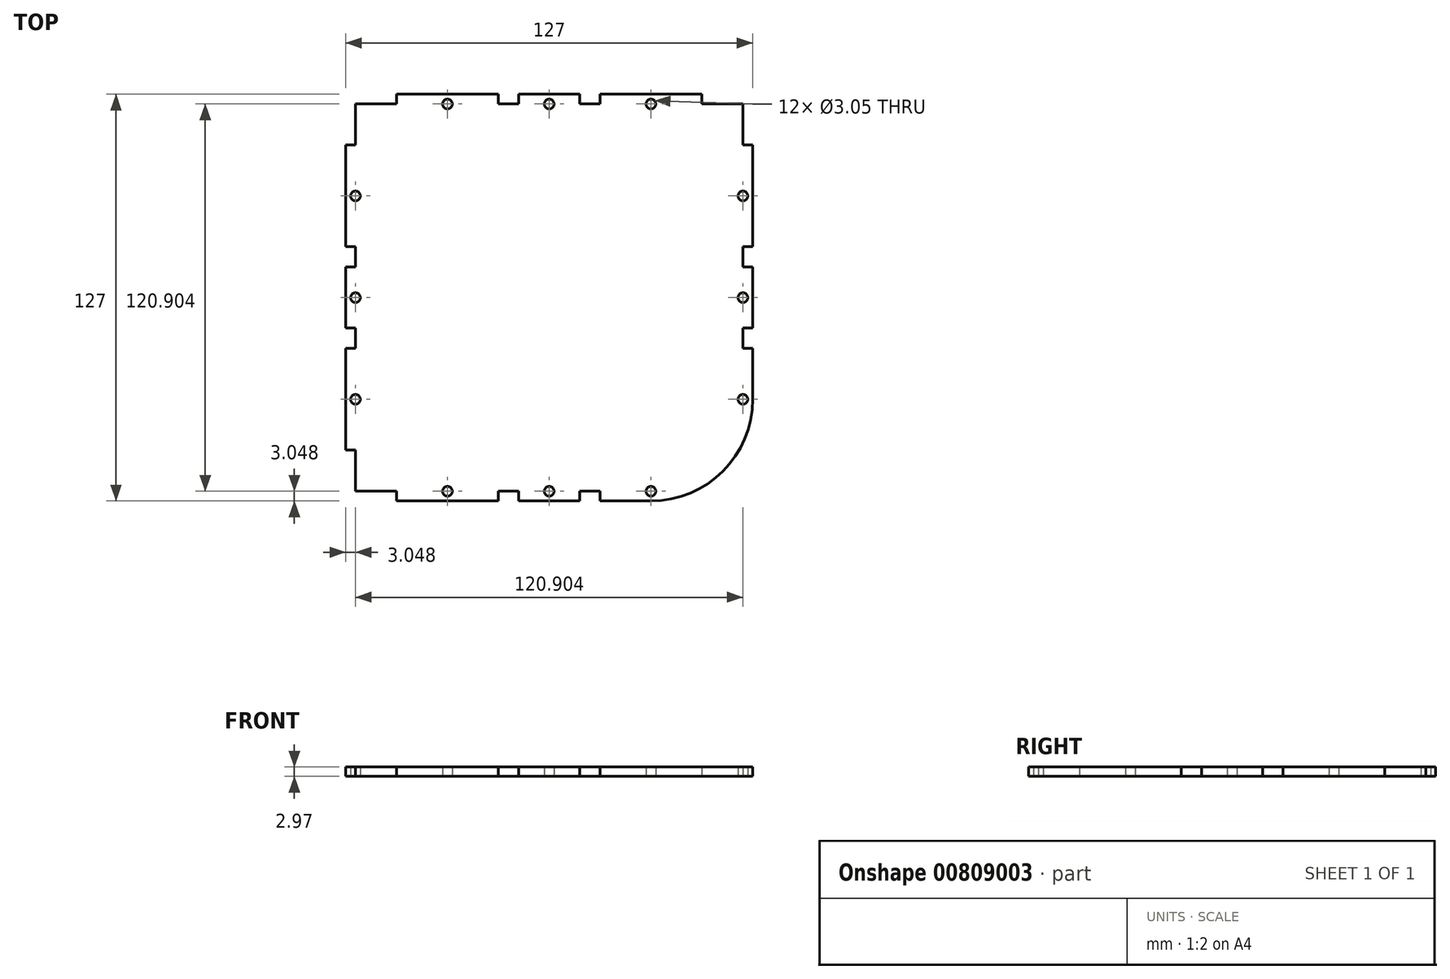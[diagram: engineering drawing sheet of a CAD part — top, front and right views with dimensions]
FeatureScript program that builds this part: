
annotation { "Feature Type Name" : "Feature", "Feature Type Description" : "" }
export const myFeature = defineFeature(function(context is Context, id is Id, definition is map)
    precondition{}
    {
        {
            var Q0;
            Q0=qCreatedBy(makeId("Top.planeOp"),FACE);
            var sketch = newSketch(context, id + "F0", { "sketchPlane" : qUnion([Q0])});
            skLineSegment(sketch, "E0", {"start": v(0, 76.16) * mm, "end": v(0, -68.5) * mm, "construction": true});
            skLineSegment(sketch, "E1", {"start": v(-81.79, 0) * mm, "end": v(75, 0) * mm, "construction": true});
            skLineSegment(sketch, "E2.right", {"start": v(63.5, 47.62) * mm, "end": v(63.5, 15.88) * mm});
            skLineSegment(sketch, "E3", {"start": v(-60.45, 78.6) * mm, "end": v(-60.45, -79.5) * mm, "construction": true});
            skLineSegment(sketch, "E4", {"start": v(-79.62, 60.45) * mm, "end": v(85.22, 60.45) * mm, "construction": true});
            skLineSegment(sketch, "E5", {"start": v(60.45, 79.72) * mm, "end": v(60.45, -47.62) * mm, "construction": true});
            skLineSegment(sketch, "E6", {"start": v(-81.64, -60.45) * mm, "end": v(47.63, -60.45) * mm, "construction": true});
            skCircle(sketch, "E7", {"center": v(0, 60.45) * mm, "radius": 1.52 * mm});
            skCircle(sketch, "E8", {"center": v(-60.45, 0) * mm, "radius": 1.52 * mm});
            skCircle(sketch, "E9", {"center": v(60.45, 0) * mm, "radius": 1.52 * mm});
            skCircle(sketch, "E10", {"center": v(0, -60.45) * mm, "radius": 1.52 * mm});
            skCircle(sketch, "E11", {"center": v(-31.75, -60.45) * mm, "radius": 1.52 * mm});
            skCircle(sketch, "E12", {"center": v(-60.45, -31.75) * mm, "radius": 1.52 * mm});
            skCircle(sketch, "E13", {"center": v(-60.45, 31.75) * mm, "radius": 1.52 * mm});
            skCircle(sketch, "E14", {"center": v(-31.75, 60.45) * mm, "radius": 1.52 * mm});
            skCircle(sketch, "E15", {"center": v(31.75, 60.45) * mm, "radius": 1.52 * mm});
            skCircle(sketch, "E16", {"center": v(60.45, 31.75) * mm, "radius": 1.52 * mm});
            skCircle(sketch, "E17", {"center": v(60.45, -31.75) * mm, "radius": 1.52 * mm});
            skCircle(sketch, "E18", {"center": v(31.75, -60.45) * mm, "radius": 1.52 * mm});
            skLineSegment(sketch, "E19", {"start": v(-47.62, 63.5) * mm, "end": v(-47.62, 60.45) * mm});
            skLineSegment(sketch, "E20", {"start": v(-47.62, 60.45) * mm, "end": v(-60.45, 60.45) * mm});
            skLineSegment(sketch, "E21", {"start": v(-60.45, 60.45) * mm, "end": v(-60.45, 47.62) * mm});
            skLineSegment(sketch, "E22", {"start": v(-60.45, 47.62) * mm, "end": v(-63.5, 47.62) * mm});
            skLineSegment(sketch, "E23", {"start": v(47.63, 63.5) * mm, "end": v(47.63, 60.45) * mm});
            skLineSegment(sketch, "E24", {"start": v(47.62, 60.45) * mm, "end": v(60.45, 60.45) * mm});
            skLineSegment(sketch, "E25", {"start": v(60.45, 60.45) * mm, "end": v(60.45, 47.62) * mm});
            skLineSegment(sketch, "E26", {"start": v(60.45, 47.62) * mm, "end": v(63.5, 47.62) * mm});
            skLineSegment(sketch, "E27", {"start": v(-60.45, -47.63) * mm, "end": v(-63.5, -47.63) * mm});
            skLineSegment(sketch, "E28", {"start": v(-47.62, -63.5) * mm, "end": v(-47.62, -60.45) * mm});
            skLineSegment(sketch, "E29", {"start": v(60.45, -60.45) * mm, "end": v(60.45, -47.62) * mm});
            skLineSegment(sketch, "E30.trimOffspring", {"start": v(-63.5, 47.62) * mm, "end": v(-63.5, 15.87) * mm});
            skLineSegment(sketch, "E31.trimOffspring", {"start": v(-47.62, 63.5) * mm, "end": v(-15.88, 63.5) * mm});
            skPoint(sketch, "E2.left.start.orphan", {"position": v(-63.5, 63.5) * mm});
            skLineSegment(sketch, "E32", {"start": v(-60.45, -47.63) * mm, "end": v(-60.45, -60.45) * mm});
            skLineSegment(sketch, "E33", {"start": v(-60.45, -60.45) * mm, "end": v(-47.62, -60.45) * mm});
            skLineSegment(sketch, "E34.trimOffspring", {"start": v(-47.62, -63.5) * mm, "end": v(-15.88, -63.5) * mm});
            skLineSegment(sketch, "E35", {"start": v(-9.53, 60.45) * mm, "end": v(-9.53, 63.5) * mm});
            skLineSegment(sketch, "E36", {"start": v(9.52, 60.45) * mm, "end": v(9.52, 63.5) * mm});
            skLineSegment(sketch, "E37", {"start": v(-15.88, 63.5) * mm, "end": v(-15.88, 60.45) * mm});
            skLineSegment(sketch, "E38", {"start": v(15.88, 63.5) * mm, "end": v(15.88, 60.45) * mm});
            skLineSegment(sketch, "E39", {"start": v(-15.88, 60.45) * mm, "end": v(-9.53, 60.45) * mm});
            skLineSegment(sketch, "E40", {"start": v(9.52, 60.45) * mm, "end": v(15.88, 60.45) * mm});
            skLineSegment(sketch, "E41.trimOffspring", {"start": v(-9.53, 63.5) * mm, "end": v(9.52, 63.5) * mm});
            skLineSegment(sketch, "E42.trimOffspring", {"start": v(15.88, 63.5) * mm, "end": v(47.62, 63.5) * mm});
            skLineSegment(sketch, "E43", {"start": v(-63.5, 15.87) * mm, "end": v(-60.45, 15.87) * mm});
            skLineSegment(sketch, "E44", {"start": v(-63.5, 9.53) * mm, "end": v(-60.45, 9.53) * mm});
            skLineSegment(sketch, "E45", {"start": v(-63.5, -9.53) * mm, "end": v(-60.45, -9.53) * mm});
            skLineSegment(sketch, "E46", {"start": v(-63.5, -15.88) * mm, "end": v(-60.45, -15.88) * mm});
            skLineSegment(sketch, "E47", {"start": v(-60.45, 15.87) * mm, "end": v(-60.45, 9.53) * mm});
            skLineSegment(sketch, "E48", {"start": v(-60.45, -9.53) * mm, "end": v(-60.45, -15.88) * mm});
            skLineSegment(sketch, "E49.trimOffspring", {"start": v(-63.5, 9.53) * mm, "end": v(-63.5, -9.53) * mm});
            skLineSegment(sketch, "E50.trimOffspring", {"start": v(-63.5, -15.88) * mm, "end": v(-63.5, -47.63) * mm});
            skLineSegment(sketch, "E51", {"start": v(-15.88, -60.45) * mm, "end": v(-15.88, -63.5) * mm});
            skLineSegment(sketch, "E52", {"start": v(-9.52, -60.45) * mm, "end": v(-9.52, -63.5) * mm});
            skLineSegment(sketch, "E53", {"start": v(9.53, -60.45) * mm, "end": v(9.53, -63.5) * mm});
            skLineSegment(sketch, "E54", {"start": v(15.88, -60.45) * mm, "end": v(15.88, -63.5) * mm});
            skLineSegment(sketch, "E55", {"start": v(9.53, -60.45) * mm, "end": v(15.88, -60.45) * mm});
            skLineSegment(sketch, "E56", {"start": v(-15.88, -60.45) * mm, "end": v(-9.52, -60.45) * mm});
            skLineSegment(sketch, "E57.trimOffspring", {"start": v(-9.52, -63.5) * mm, "end": v(9.53, -63.5) * mm});
            skLineSegment(sketch, "E58.trimOffspring", {"start": v(15.88, -63.5) * mm, "end": v(31.75, -63.5) * mm});
            skLineSegment(sketch, "E59", {"start": v(63.5, 15.88) * mm, "end": v(60.45, 15.88) * mm});
            skLineSegment(sketch, "E60", {"start": v(60.45, 9.53) * mm, "end": v(63.5, 9.53) * mm});
            skLineSegment(sketch, "E61", {"start": v(63.5, -9.53) * mm, "end": v(60.45, -9.53) * mm});
            skLineSegment(sketch, "E62", {"start": v(60.45, -15.88) * mm, "end": v(63.5, -15.88) * mm});
            skLineSegment(sketch, "E63", {"start": v(60.45, 15.88) * mm, "end": v(60.45, 9.53) * mm});
            skLineSegment(sketch, "E64", {"start": v(60.45, -9.53) * mm, "end": v(60.45, -15.88) * mm});
            skLineSegment(sketch, "E65.trimOffspring", {"start": v(63.5, 9.53) * mm, "end": v(63.5, -9.53) * mm});
            skLineSegment(sketch, "E66.trimOffspring", {"start": v(63.5, -15.88) * mm, "end": v(63.5, -31.75) * mm});
            skLineSegment(sketch, "E67", {"start": v(63.5, -47.62) * mm, "end": v(63.5, -83.47) * mm, "construction": true});
            skLineSegment(sketch, "E68", {"start": v(47.63, -63.5) * mm, "end": v(87.74, -63.5) * mm, "construction": true});
            skLineSegment(sketch, "E69", {"start": v(0, 0) * mm, "end": v(63.5, -63.5) * mm, "construction": true});
            skArc(sketch, "E70", {"start": v(31.75, -63.5) * mm, "mid": v(54.2, -54.2) * mm, "end": v(63.5, -31.75) * mm});
            skLineSegment(sketch, "E71.trimOffspring", {"start": v(60.45, -60.45) * mm, "end": v(84.77, -60.45) * mm, "construction": true});
            skLineSegment(sketch, "E72.trimOffspring", {"start": v(60.45, -60.45) * mm, "end": v(60.45, -81.3) * mm, "construction": true});
            skSolve(sketch);
        }
        {
            var Q0;
            Q0 = qSketchRegion(id + "F0", true);
            extrude(context, id + "F1", {"entities" : qUnion([Q0]), "depth" : 2.97 * mm, "offsetDistance" : 25.4 * mm});
        }
    });
